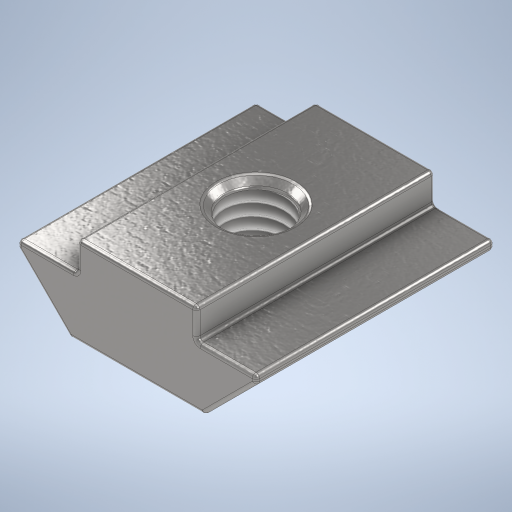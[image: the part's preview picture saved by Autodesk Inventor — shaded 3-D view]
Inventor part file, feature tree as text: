
AUTODESK INVENTOR PART (.ipt)
format: ipt  version: 2024 (Build 280153000, 153)  size: 397,312 bytes
history: native  units: mm
features: chamfer x2, sketch x2, extrude x1, hole x1, fillet x1
ambient origin geometry x8: Origin, YZ Plane, XZ Plane, XY Plane, X Axis, Y Axis, Z Axis, Center Point
bodies: Solid1 (feature_tree)
feature tree (7):
  extrude  "Extrusion1"  Depth=4.0mm
  chamfer  "Chamfer1"  Distance=8.0mm
  hole  "Hole1"  [1 undecoded]
  chamfer  "Chamfer2"  Distance=2.0mm Angle=45.0deg
  fillet  "Fillet1"  Radius=0.5mm
  sketch  "Sketch1"  dims[d0=2.0mm d1=4.0mm]
  sketch  "Sketch2"  dims[d2=16.0mm d3=8.0mm d4=16.0mm d5=0.0mm d6=3.5mm d7=2.0mm d8=45.0deg d9=4.134mm d10=10.0mm d11=4.0mm d12=2.0mm d13=90.0deg d14=8.0mm d15=20.594885mm d16=0.5mm d17=2.0mm d18=45.0deg d19=0.25mm]
note: 1 required parameter value undecoded (feature->parameter linkage not recoverable at this tier; creation-order binding heuristic only, values carry confidence <= 0.55)
